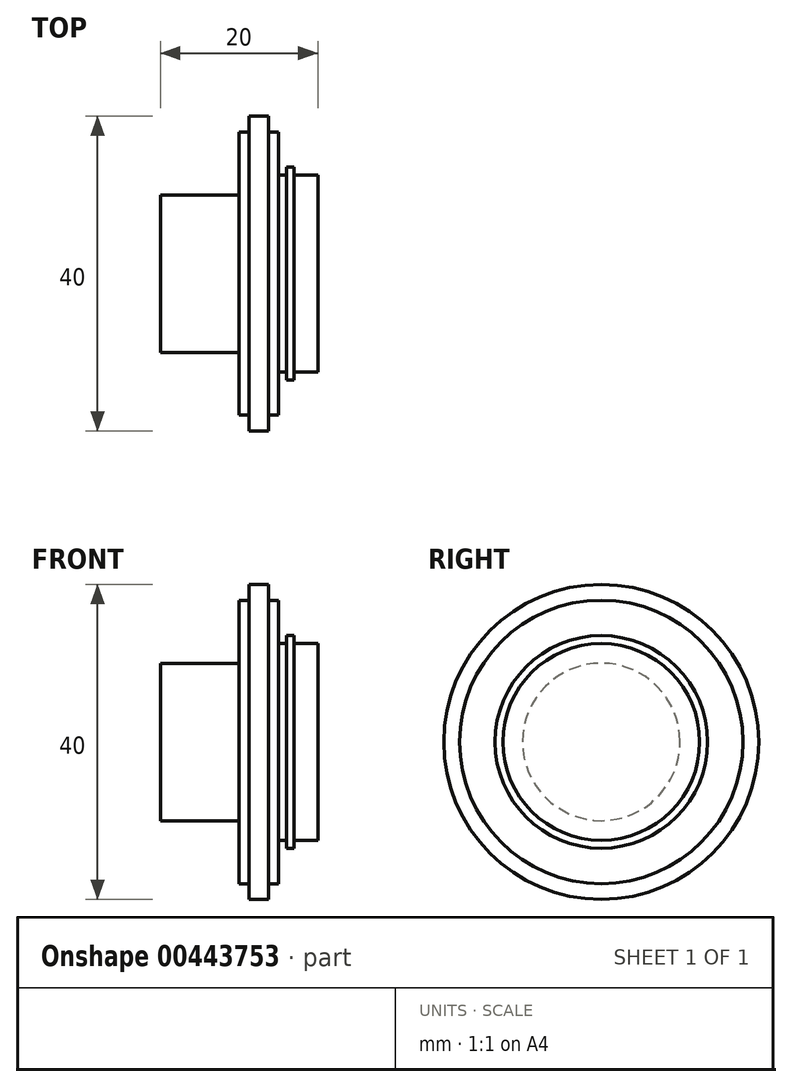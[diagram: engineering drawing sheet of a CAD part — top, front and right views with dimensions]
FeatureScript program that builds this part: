
annotation { "Feature Type Name" : "Feature", "Feature Type Description" : "" }
export const myFeature = defineFeature(function(context is Context, id is Id, definition is map)
    precondition{}
    {
        {
            var Q0;
            Q0=qCreatedBy(makeId("Front.planeOp"),FACE);
            var sketch = newSketch(context, id + "F0", { "sketchPlane" : qUnion([Q0])});
            skLineSegment(sketch, "E0", {"start": v(0, 0) * mm, "end": v(-20, 0) * mm});
            skLineSegment(sketch, "E1", {"start": v(-20, 0) * mm, "end": v(-20, 10) * mm});
            skLineSegment(sketch, "E2", {"start": v(-20, 10) * mm, "end": v(-10, 10) * mm});
            skLineSegment(sketch, "E3", {"start": v(-10, 10) * mm, "end": v(-10, 18) * mm});
            skLineSegment(sketch, "E4", {"start": v(-10, 18) * mm, "end": v(-8.75, 18) * mm});
            skLineSegment(sketch, "E5", {"start": v(-8.75, 18) * mm, "end": v(-8.75, 20) * mm});
            skLineSegment(sketch, "E6", {"start": v(-8.75, 20) * mm, "end": v(-6.25, 20) * mm});
            skLineSegment(sketch, "E7", {"start": v(-6.25, 20) * mm, "end": v(-6.25, 18) * mm});
            skLineSegment(sketch, "E8", {"start": v(-6.25, 18) * mm, "end": v(-5, 18) * mm});
            skLineSegment(sketch, "E9", {"start": v(-5, 18) * mm, "end": v(-5, 12.5) * mm});
            skLineSegment(sketch, "E10", {"start": v(-5, 12.5) * mm, "end": v(-4, 12.5) * mm});
            skLineSegment(sketch, "E11", {"start": v(-4, 12.5) * mm, "end": v(-4, 13.5) * mm});
            skLineSegment(sketch, "E12", {"start": v(-4, 13.5) * mm, "end": v(-3, 13.5) * mm});
            skLineSegment(sketch, "E13", {"start": v(-3, 13.5) * mm, "end": v(-3, 12.5) * mm});
            skLineSegment(sketch, "E14", {"start": v(-3, 12.5) * mm, "end": v(0, 12.5) * mm});
            skLineSegment(sketch, "E15", {"start": v(0, 12.5) * mm, "end": v(0, 0) * mm});
            skSolve(sketch);
        }
        {
            var Q0;
            Q0=makeQuery(id+"F0.imprint","IMPRINT",FACE,{"disambiguationData":[TD([[makeQuery(id+"F0.imprint","IMPRINT",EDGE,{"derivedFrom":sQuery(id+"F0.wireOp",EDGE,"E0")}),-1.0]])]});
            var Q1;
            Q1=sQuery(id+"F0.wireOp",EDGE,"E0");
            revolve(context, id + "F1", {"entities" : qUnion([Q0]), "axis" : qUnion([Q1]), "revolveType" : RevolveType.FULL});
        }
    });
